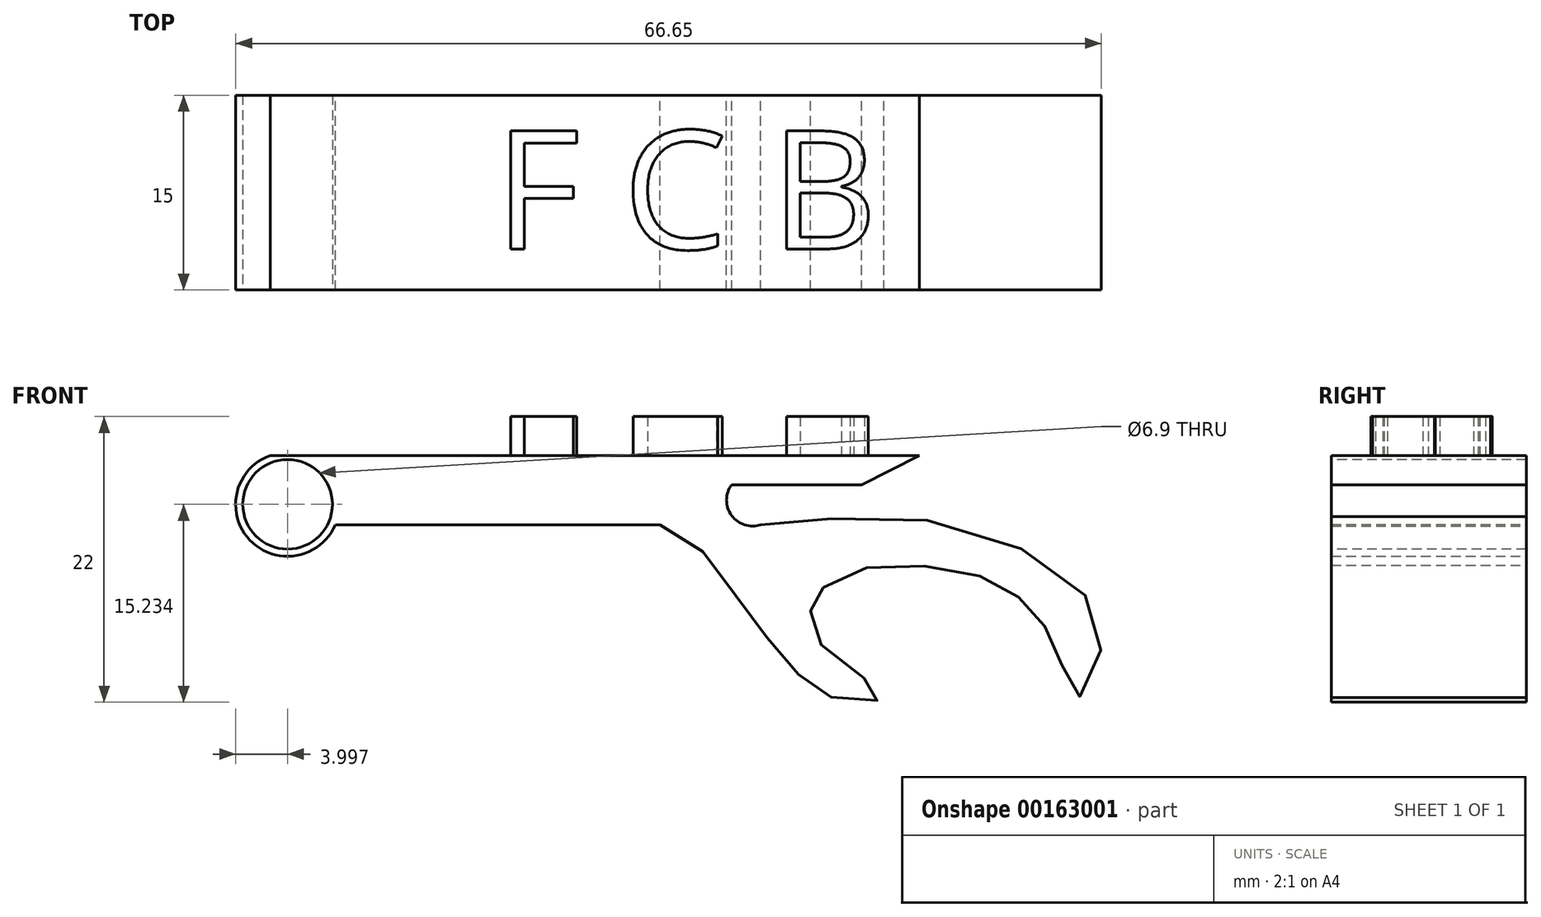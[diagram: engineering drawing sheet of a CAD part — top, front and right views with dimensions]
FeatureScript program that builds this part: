
annotation { "Feature Type Name" : "Feature", "Feature Type Description" : "" }
export const myFeature = defineFeature(function(context is Context, id is Id, definition is map)
    precondition{}
    {
        {
            var Q0;
            Q0=qCreatedBy(makeId("Front.planeOp"),FACE);
            var sketch = newSketch(context, id + "F0", { "sketchPlane" : qUnion([Q0])});
            skLineSegment(sketch, "E0", {"start": v(0, 0) * mm, "end": v(50, 0) * mm});
            skLineSegment(sketch, "E1", {"start": v(10.74, 0) * mm, "end": v(10.74, -5) * mm});
            skLineSegment(sketch, "E2", {"start": v(5.03, -5.34) * mm, "end": v(30.03, -5.34) * mm});
            skArc(sketch, "E3", {"start": v(0, 0) * mm, "mid": v(-1.57, -6.5) * mm, "end": v(5.03, -5.34) * mm});
            skLineSegment(sketch, "E4", {"start": v(50, 0) * mm, "end": v(45.54, -2.25) * mm});
            skLineSegment(sketch, "E5", {"start": v(45.54, -2.25) * mm, "end": v(35.54, -2.25) * mm});
            skFitSpline(sketch, "E6", {"points": [v(30.03, -5.34) * mm, v(33.75, -7.95) * mm, v(36.7, -11.99) * mm, v(39.57, -15.65) * mm, v(41.87, -17.9) * mm, v(44.66, -18.95) * mm, v(47.25, -18.56) * mm, v(44.36, -16.25) * mm, v(41.8, -13.55) * mm, v(41.64, -11.7) * mm, v(41.96, -10.86) * mm, v(44.22, -9.13) * mm, v(49.45, -8.46) * mm, v(54.84, -9.36) * mm, v(57.74, -11) * mm, v(59.55, -13.03) * mm, v(60.83, -15.65) * mm, v(62.03, -18.65) * mm, v(63.83, -15.65) * mm, v(62.33, -10.26) * mm, v(49.38, -4.85) * mm, v(37.78, -5.34) * mm], "startDerivative": vector(83.52, 12.75) * mm, "endDerivative": vector(-88.92, 0.2) * mm});
            skArc(sketch, "E7", {"start": v(35.54, -2.25) * mm, "mid": v(35.52, -4.62) * mm, "end": v(37.78, -5.34) * mm});
            skSolve(sketch);
        }
        {
            var Q0;
            Q0 = qSketchRegion(id + "F0", true);
            extrude(context, id + "F1", {"entities" : qUnion([Q0]), "depth" : 15 * mm});
        }
        {
            var Q0;
            Q0=makeQuery(id+"F1.opExtrude","CAP_FACE",FACE,{"disambiguationData":[OSD([sQuery(id+"F0.wireOp",EDGE,"E0"),sQuery(id+"F0.wireOp",EDGE,"E2"),sQuery(id+"F0.wireOp",EDGE,"E3"),sQuery(id+"F0.wireOp",EDGE,"E4"),sQuery(id+"F0.wireOp",EDGE,"E5"),sQuery(id+"F0.wireOp",EDGE,"E6"),sQuery(id+"F0.wireOp",EDGE,"E7")])],"isStart":false});
            var sketch = newSketch(context, id + "F2", { "sketchPlane" : qUnion([Q0])});
            skCircle(sketch, "E8", {"center": v(1.35, -3.77) * mm, "radius": 3.45 * mm});
            skSolve(sketch);
        }
        {
            var Q0;
            Q0 = qSketchRegion(id + "F2", true);
            extrude(context, id + "F3", {"entities" : qUnion([Q0]), "operationType" : NewBodyOperationType.REMOVE, "oppositeDirection" : true, "depth" : 25 * mm});
        }
        {
            var Q0;
            Q0=makeQuery(id+"F1.opExtrude","SWEPT_FACE",FACE,{"disambiguationData":[OSD([sQuery(id+"F0.wireOp",EDGE,"E0")])]});
            var sketch = newSketch(context, id + "F4", { "sketchPlane" : qUnion([Q0])});
            skText(sketch, "E9", { "text": "F C B", "fontName": "OpenSans-Regular.ttf"});
            const initialGuessF4  = {"E9": [0.01728, -0.01184, 1, 0, 0.00917]};
            skSetInitialGuess(sketch, initialGuessF4);
            skSolve(sketch);
        }
        {
            var Q0;
            Q0 = qSketchRegion(id + "F4", true);
            extrude(context, id + "F5", {"entities" : qUnion([Q0]), "operationType" : NewBodyOperationType.ADD, "depth" : 3 * mm});
        }
    });
